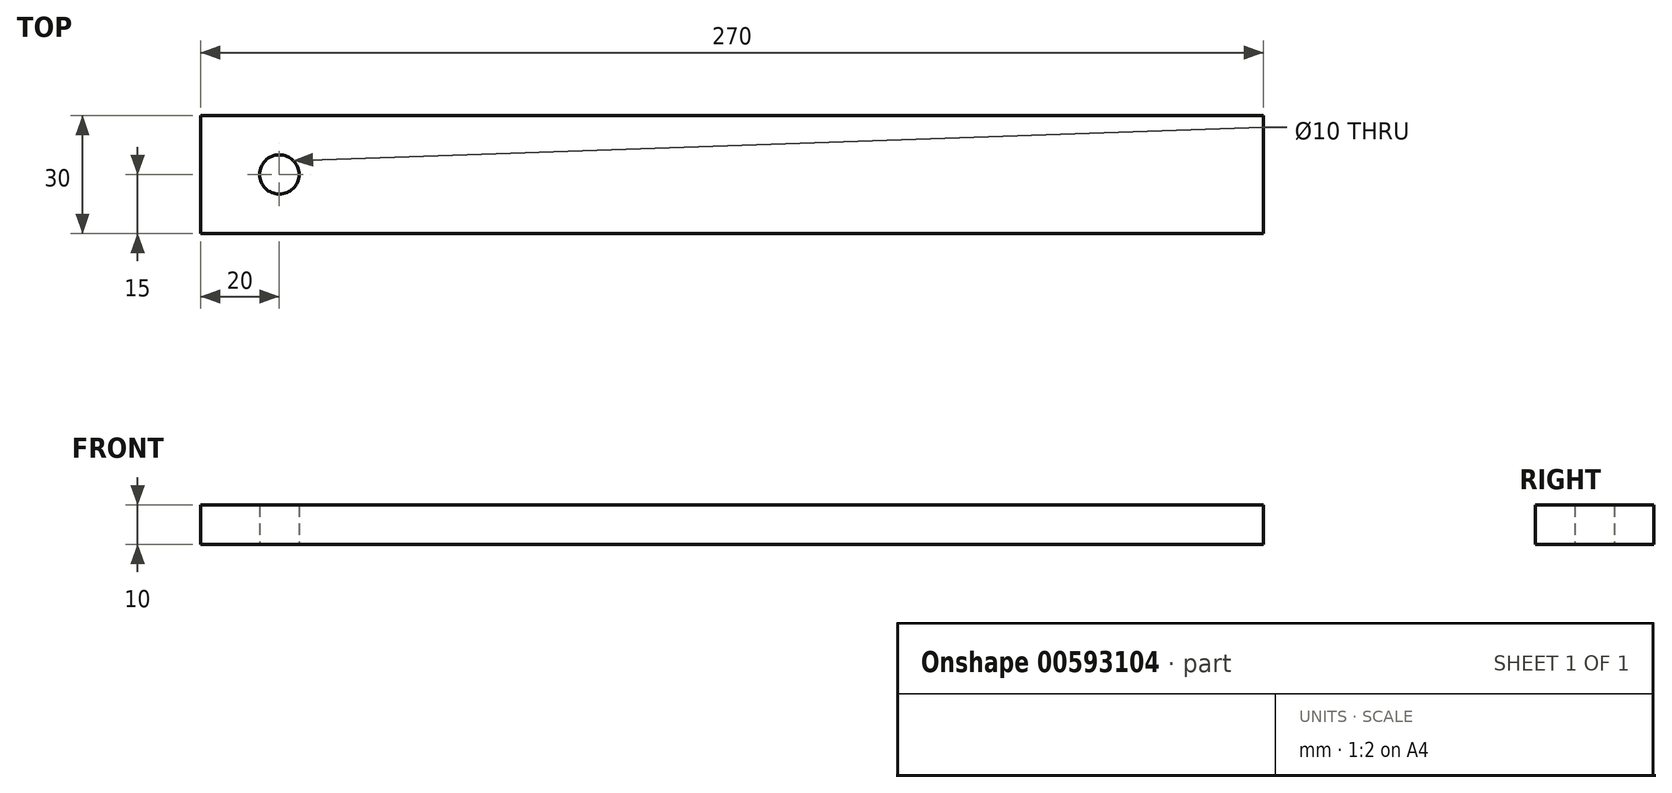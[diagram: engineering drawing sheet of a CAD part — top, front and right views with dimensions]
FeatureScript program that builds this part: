
annotation { "Feature Type Name" : "Feature", "Feature Type Description" : "" }
export const myFeature = defineFeature(function(context is Context, id is Id, definition is map)
    precondition{}
    {
        {
            var Q0;
            Q0=qCreatedBy(makeId("Top.planeOp"),FACE);
            var sketch = newSketch(context, id + "F0", { "sketchPlane" : qUnion([Q0])});
            skLineSegment(sketch, "E0.bottom", {"start": v(135, 15) * mm, "end": v(-135, 15) * mm});
            skLineSegment(sketch, "E0.top", {"start": v(135, -15) * mm, "end": v(-135, -15) * mm});
            skLineSegment(sketch, "E0.left", {"start": v(135, 15) * mm, "end": v(135, -15) * mm});
            skLineSegment(sketch, "E0.right", {"start": v(-135, 15) * mm, "end": v(-135, -15) * mm});
            skPoint(sketch, "E0.middle", {"position": v(0, 0) * mm});
            skCircle(sketch, "E1", {"center": v(-115, 0) * mm, "radius": 5 * mm});
            skSolve(sketch);
        }
        {
            var Q0;
            Q0=makeQuery(id+"F0.imprint","IMPRINT",FACE,{"disambiguationData":[TD([[makeQuery(id+"F0.imprint","IMPRINT",EDGE,{"derivedFrom":sQuery(id+"F0.wireOp",EDGE,"E0.bottom")}),1.0]])]});
            extrude(context, id + "F1", {"entities" : qUnion([Q0]), "depth" : 10 * mm, "offsetDistance" : 25 * mm});
        }
    });
